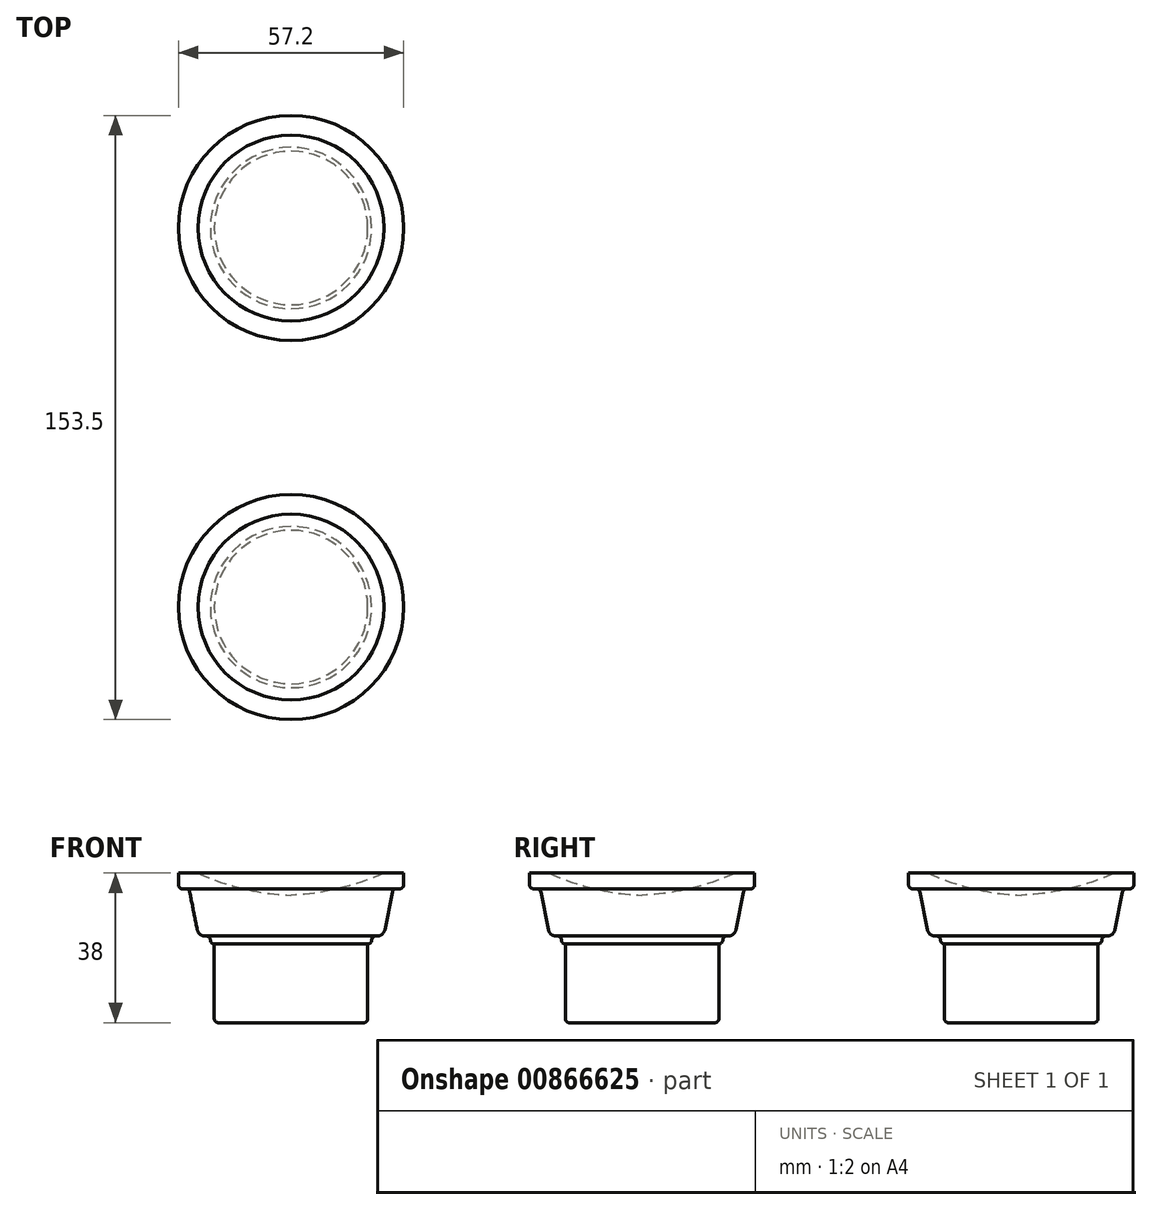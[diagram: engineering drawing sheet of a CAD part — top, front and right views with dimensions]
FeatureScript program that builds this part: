
annotation { "Feature Type Name" : "Feature", "Feature Type Description" : "" }
export const myFeature = defineFeature(function(context is Context, id is Id, definition is map)
    precondition{}
    {
        {
            var Q0;
            Q0=qCreatedBy(makeId("Front.planeOp"),FACE);
            var sketch = newSketch(context, id + "F0", { "sketchPlane" : qUnion([Q0])});
            skLineSegment(sketch, "E0", {"start": v(0, 0) * mm, "end": v(19.5, 0) * mm});
            skLineSegment(sketch, "E1", {"start": v(19.5, 0) * mm, "end": v(19.5, 20) * mm});
            skLineSegment(sketch, "E2", {"start": v(19.5, 20) * mm, "end": v(20.5, 20) * mm});
            skLineSegment(sketch, "E3", {"start": v(20.5, 20) * mm, "end": v(20.5, 22) * mm});
            skLineSegment(sketch, "E4", {"start": v(28.6, 38) * mm, "end": v(28.6, 34) * mm});
            skLineSegment(sketch, "E5", {"start": v(20.5, 22) * mm, "end": v(23.5, 22) * mm});
            skLineSegment(sketch, "E6", {"start": v(28.6, 34) * mm, "end": v(25.9, 34) * mm});
            skLineSegment(sketch, "E7", {"start": v(23.5, 22) * mm, "end": v(25.9, 34) * mm});
            skPoint(sketch, "E8", {"position": v(0, 32.36) * mm});
            skPoint(sketch, "E9", {"position": v(23.6, 38) * mm});
            skLineSegment(sketch, "E10", {"start": v(23.6, 38) * mm, "end": v(28.6, 38) * mm});
            skLineSegment(sketch, "E11", {"start": v(0, 0) * mm, "end": v(0, 32.36) * mm});
            skFitSpline(sketch, "E12", {"points": [v(23.6, 38) * mm, v(0, 32.36) * mm], "startDerivative": vector(-16.3, -7.85) * mm, "endDerivative": vector(-26.79, -0.96) * mm});
            skSolve(sketch);
        }
        {
            var Q0;
            Q0=makeQuery(id+"F0.imprint","IMPRINT",FACE,{"disambiguationData":[TD([[makeQuery(id+"F0.imprint","IMPRINT",EDGE,{"derivedFrom":sQuery(id+"F0.wireOp",EDGE,"E0")}),1.0]])]});
            var Q1;
            Q1=sQuery(id+"F0.wireOp",EDGE,"E11");
            revolve(context, id + "F1", {"surfaceOperationType" : NewSurfaceOperationType.NEW, "entities" : qUnion([Q0]), "axis" : qUnion([Q1]), "revolveType" : RevolveType.FULL});
        }
        {
            var Q0;
            Q0=makeQuery(id+"F1.opRevolve","SWEPT_EDGE",EDGE,{"disambiguationData":[OSD([sQuery(id+"F0.wireOp",EDGE,"E0"),sQuery(id+"F0.wireOp",EDGE,"E1")])]});
            fillet(context, id + "F2", {"entities" : qUnion([Q0]), "radius" : 1 * mm, "tangentPropagation" : true, "allowEdgeOverflow" : false});
        }
        {
            var Q0;
            Q0=makeQuery(id+"F1.opRevolve","SWEPT_EDGE",EDGE,{"disambiguationData":[OSD([sQuery(id+"F0.wireOp",EDGE,"E5"),sQuery(id+"F0.wireOp",EDGE,"E7")])]});
            fillet(context, id + "F3", {"entities" : qUnion([Q0]), "radius" : 2 * mm, "tangentPropagation" : true, "allowEdgeOverflow" : false});
        }
        {
            var Q0;
            Q0=makeQuery(id+"F1.opRevolve","SWEPT_EDGE",EDGE,{"disambiguationData":[OSD([sQuery(id+"F0.wireOp",EDGE,"E4"),sQuery(id+"F0.wireOp",EDGE,"E6")])]});
            fillet(context, id + "F4", {"entities" : qUnion([Q0]), "radius" : 1 * mm, "tangentPropagation" : true, "allowEdgeOverflow" : false});
        }
        {
            var Q0;
            Q0=makeQuery(id+"F1.opRevolve","SWEPT_EDGE",EDGE,{"disambiguationData":[OSD([sQuery(id+"F0.wireOp",EDGE,"E6"),sQuery(id+"F0.wireOp",EDGE,"E7")])]});
            fillet(context, id + "F5", {"entities" : qUnion([Q0]), "radius" : 1 * mm, "tangentPropagation" : true, "allowEdgeOverflow" : false});
        }
        {
            var Q0;
            Q0=makeQuery(id+"F1.opRevolve","SWEPT_EDGE",EDGE,{"disambiguationData":[OSD([sQuery(id+"F0.wireOp",EDGE,"E2"),sQuery(id+"F0.wireOp",EDGE,"E3")])]});
            fillet(context, id + "F6", {"entities" : qUnion([Q0]), "radius" : 1 * mm, "tangentPropagation" : true, "allowEdgeOverflow" : false});
        }
        {
            var Q0;
            Q0=makeQuery(id+"F1.opRevolve","SWEPT_EDGE",EDGE,{"disambiguationData":[OSD([sQuery(id+"F0.wireOp",EDGE,"E3"),sQuery(id+"F0.wireOp",EDGE,"E5")])]});
            fillet(context, id + "F7", {"entities" : qUnion([Q0]), "radius" : 1 * mm, "tangentPropagation" : true, "allowEdgeOverflow" : false});
        }
        {
            var Q0;
            Q0=makeQuery(id+"F1.opRevolve","SWEPT_BODY",BODY,{"disambiguationData":[OSD([sQuery(id+"F0.wireOp",EDGE,"E0"),sQuery(id+"F0.wireOp",EDGE,"E1"),sQuery(id+"F0.wireOp",EDGE,"E2"),sQuery(id+"F0.wireOp",EDGE,"E3"),sQuery(id+"F0.wireOp",EDGE,"E4"),sQuery(id+"F0.wireOp",EDGE,"E5"),sQuery(id+"F0.wireOp",EDGE,"E6"),sQuery(id+"F0.wireOp",EDGE,"E7"),sQuery(id+"F0.wireOp",EDGE,"E10"),sQuery(id+"F0.wireOp",EDGE,"E11"),sQuery(id+"F0.wireOp",EDGE,"E12")])]});
            transform(context, id + "F8", {"entities" : qUnion([Q0]), "transformType" : TransformType.TRANSLATION_3D, "dx" : 0 * mm, "dy" : 96.3 * mm, "dz" : 0 * mm, "makeCopy" : true});
        }
    });
